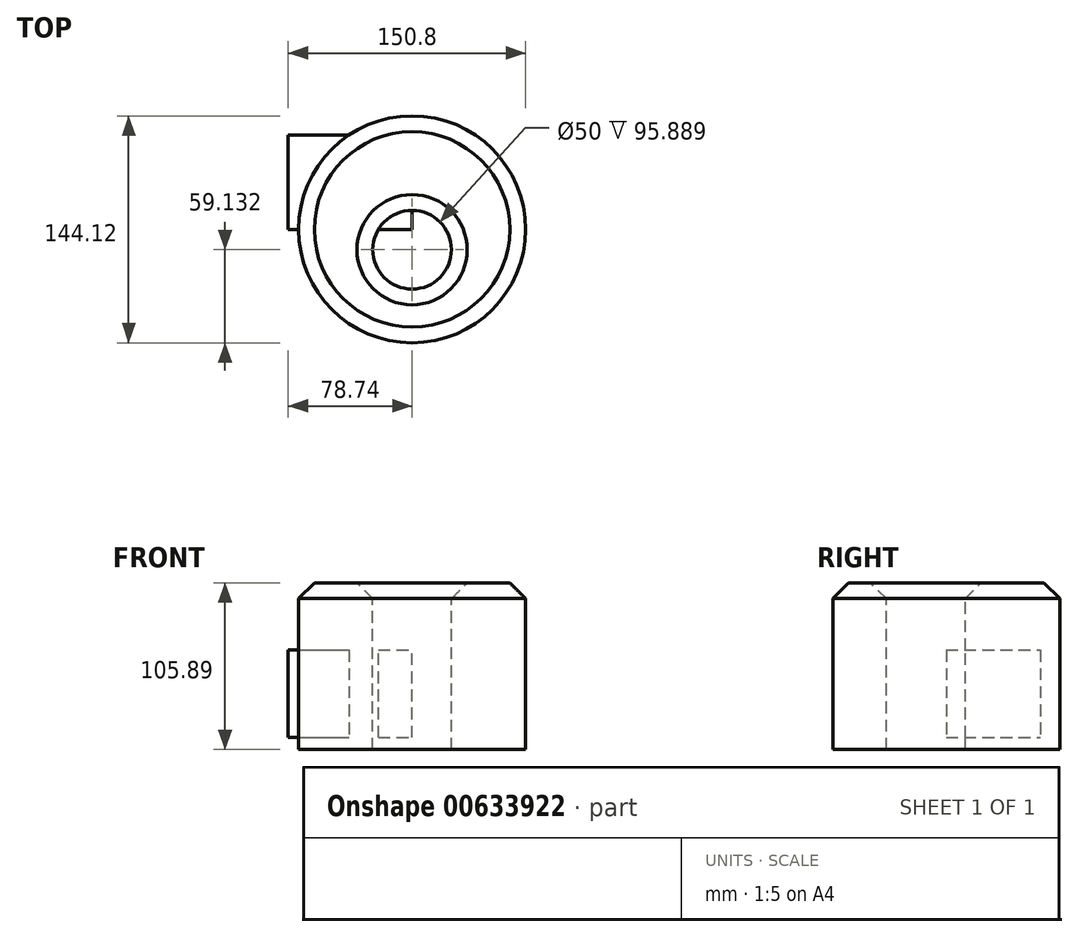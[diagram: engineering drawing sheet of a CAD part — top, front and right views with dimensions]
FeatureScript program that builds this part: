
annotation { "Feature Type Name" : "Feature", "Feature Type Description" : "" }
export const myFeature = defineFeature(function(context is Context, id is Id, definition is map)
    precondition{}
    {
        {
            var Q0;
            Q0=qCreatedBy(makeId("Top.planeOp"),FACE);
            var sketch = newSketch(context, id + "F0", { "sketchPlane" : qUnion([Q0])});
            skCircle(sketch, "E0", {"center": v(0, 0) * mm, "radius": 72.06 * mm});
            skSolve(sketch);
        }
        {
            var Q0;
            Q0 = qSketchRegion(id + "F0", true);
            extrude(context, id + "F1", {"entities" : qUnion([Q0]), "depth" : 105.89 * mm, "offsetDistance" : 25.4 * mm});
        }
        {
            var Q0;
            Q0=makeQuery(id+"F1.opExtrude","CAP_FACE",FACE,{"disambiguationData":[OSD([sQuery(id+"F0.wireOp",EDGE,"E0")])],"isStart":false});
            var sketch = newSketch(context, id + "F2", { "sketchPlane" : qUnion([Q0])});
            skCircle(sketch, "E1", {"center": v(0, -12.93) * mm, "radius": 43.25 * mm});
            skSolve(sketch);
        }
        {
            var Q0;
            Q0=sQuery(id+"F2.wireOp",VERTEX,"E1.center");
            var Q1;
            Q1=makeQuery(id+"F1.opExtrude","SWEPT_BODY",BODY,{"disambiguationData":[OSD([sQuery(id+"F0.wireOp",EDGE,"E0")])]});
            hole(context, id + "F3", {"style" : HoleStyle.SIMPLE, "endStyle" : HoleEndStyle.THROUGH, "holeDiameter" : 50 * mm, "majorDiameter" : 6.35 * mm, "isTappedThrough" : true, "tappedDepth" : 12.7 * mm, "tapClearance" : 3, "locations" : qUnion([Q0]), "scope" : qUnion([Q1])});
        }
        {
            var Q0;
            Q0=makeQuery(id+"F1.opExtrude","CAP_FACE",FACE,{"disambiguationData":[OSD([sQuery(id+"F0.wireOp",EDGE,"E0")])],"isStart":false});
            chamfer(context, id + "F4", {"entities" : qUnion([Q0]), "width" : 10 * mm, "tangentPropagation" : true});
        }
        {
            var Q0;
            Q0=qCreatedBy(makeId("Right.planeOp"),FACE);
            var sketch = newSketch(context, id + "F5", { "sketchPlane" : qUnion([Q0])});
            skLineSegment(sketch, "E2.bottom", {"start": v(0, 63.18) * mm, "end": v(59.82, 63.18) * mm});
            skLineSegment(sketch, "E2.top", {"start": v(0, 7.69) * mm, "end": v(59.82, 7.69) * mm});
            skLineSegment(sketch, "E2.left", {"start": v(0, 63.18) * mm, "end": v(0, 7.69) * mm});
            skLineSegment(sketch, "E2.right", {"start": v(59.82, 63.18) * mm, "end": v(59.82, 7.69) * mm});
            skSolve(sketch);
        }
        {
            var Q0;
            Q0 = qSketchRegion(id + "F5", true);
            extrude(context, id + "F6", {"entities" : qUnion([Q0]), "operationType" : NewBodyOperationType.ADD, "oppositeDirection" : true, "depth" : 78.74 * mm, "offsetDistance" : 25.4 * mm});
        }
    });
